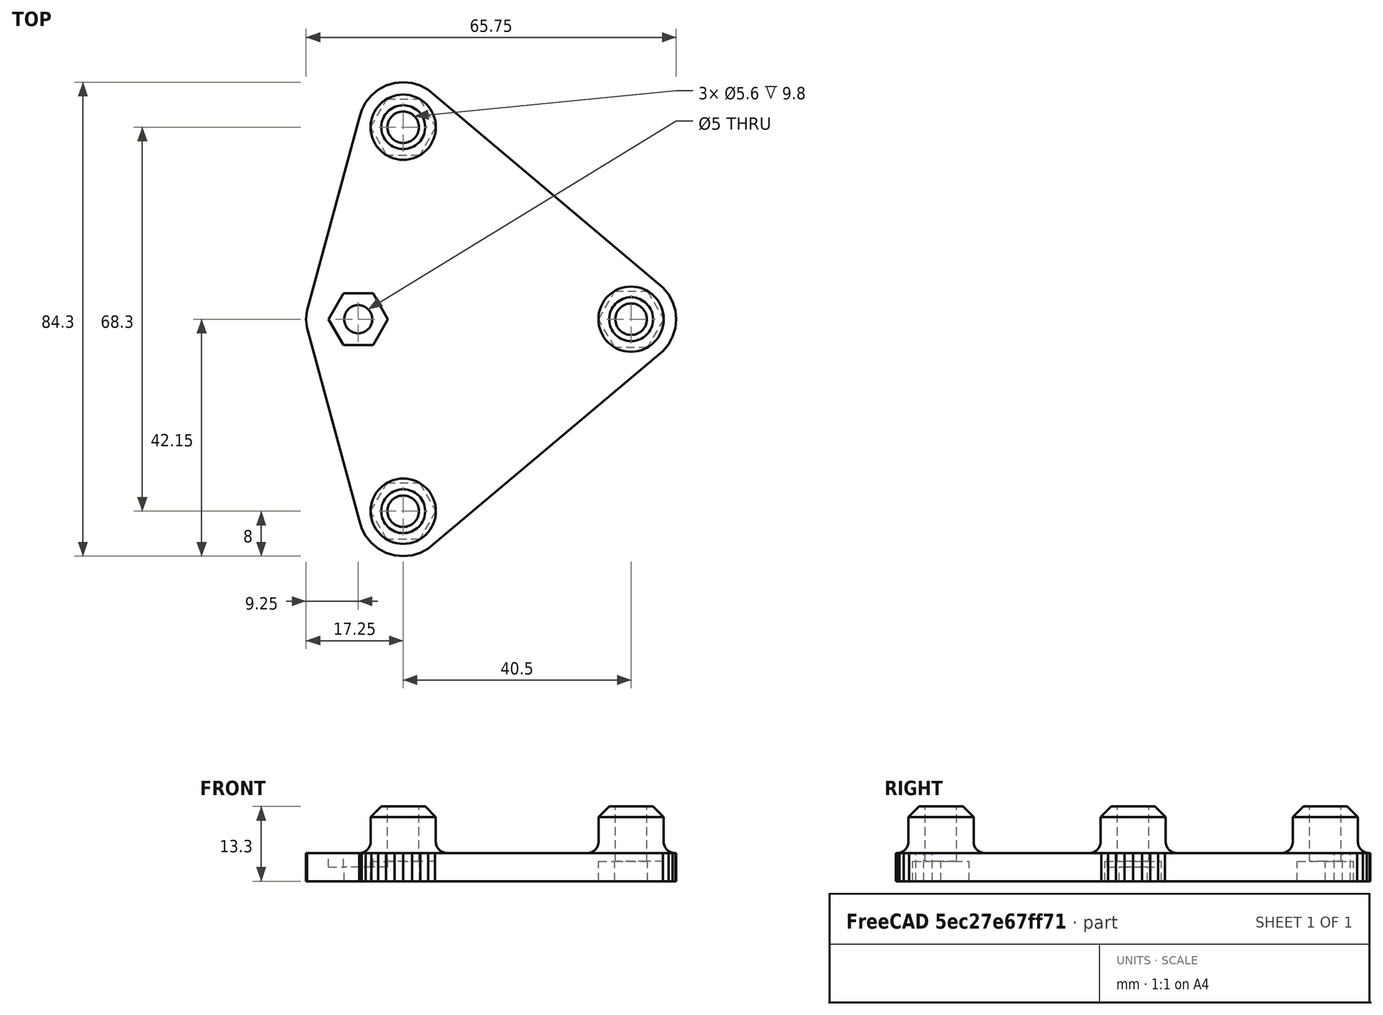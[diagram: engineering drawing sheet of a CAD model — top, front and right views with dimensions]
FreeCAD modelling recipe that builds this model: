
FCSTD DOCUMENT  (FreeCAD 0.19R24267 +99 (Git))
Label: carroZ_3_V1
License: All rights reserved
LicenseURL: http://en.wikipedia.org/wiki/All_rights_reserved
objects: Part::Feature×37, Part::Cylinder×7, Part::Cut×5, Part::Part2DObjectPython×4, Part::MultiFuse×4, Part::Prism×4, Part::Chamfer×3, Part::Fillet×3, Part::FeaturePython×2, Part::Extrusion×1, Part::Box×1, Part::Common×1, App::DocumentObjectGroupPython×1, Part::Refine×1
note: 73 computed .brp shape members not serialized (recipe doc carries the construction recipe); baked Part::Feature solids carry a one-line shape summary decoded from their .brp

FEATURE [Part::Feature] polygon
  shape: bbox 49.75 x 68.3 x 2e-07 mm, 1 faces, 0 solids (baked)
FEATURE [Part::Part2DObjectPython] circle  # Draft 2D object (typed FeaturePython)
  Area = 201.062
  FirstAngle = 0
  LastAngle = 0
  MakeFace = true
  Radius = 8
FEATURE [Part::FeaturePython] minkowski  # WARN: FeaturePython — macro-defined, semantics opaque (R4)
  Arguments = {'convexity': '0'}
  Children = -> [polygon,circle]
  Operation = minkowski
FEATURE [Part::Part2DObjectPython] circle001  # Draft 2D object (typed FeaturePython)
  Area = 24.6301
  FirstAngle = 0
  LastAngle = 0
  MakeFace = true
  Placement = pos=(-20.25,-34.15,0) rot=(0,0,1;0rad)
  Radius = 2.8
FEATURE [Part::Part2DObjectPython] circle002  # Draft 2D object (typed FeaturePython)
  Area = 24.6301
  FirstAngle = 0
  LastAngle = 0
  MakeFace = true
  Placement = pos=(-20.25,34.15,0) rot=(0,0,1;0rad)
  Radius = 2.8
FEATURE [Part::Part2DObjectPython] circle003  # Draft 2D object (typed FeaturePython)
  Area = 24.6301
  FirstAngle = 0
  LastAngle = 0
  MakeFace = true
  Placement = pos=(20.25,0,0) rot=(0,0,1;0rad)
  Radius = 2.8
FEATURE [Part::MultiFuse] union
  Shapes = -> [circle001,circle002,circle003]
FEATURE [Part::Cut] difference
  Base = -> minkowski
  Tool = -> union
FEATURE [Part::FeaturePython] RefineLinearExtrude  # WARN: FeaturePython — macro-defined, semantics opaque (R4)
  Base = -> difference
FEATURE [Part::Extrusion] LinearExtrude
  Base = -> RefineLinearExtrude
  Dir = (0,0,5)
  DirMode = 0
  FaceMakerClass = Part::FaceMakerBullseye
  LengthFwd = 0
  LengthRev = 0
  Solid = false
  Symmetric = false
FEATURE [Part::Cylinder] cylinder
  Angle = 360
  AttacherType = Attacher::AttachEngine3D
  Height = 13.3
  Radius = 5.8
FEATURE [Part::Cylinder] cylinder001
  Angle = 360
  AttacherType = Attacher::AttachEngine3D
  Height = 53.2
  Placement = pos=(0,0,-26.6) rot=(0,0,1;0rad)
  Radius = 2.8
FEATURE [Part::Cut] difference001
  Base = -> cylinder
  Placement = pos=(-20.25,-34.15,0) rot=(0,0,1;0rad)
  Tool = -> cylinder001
FEATURE [Part::Cylinder] cylinder002
  Angle = 360
  AttacherType = Attacher::AttachEngine3D
  Height = 13.3
  Radius = 5.8
FEATURE [Part::Cylinder] cylinder003
  Angle = 360
  AttacherType = Attacher::AttachEngine3D
  Height = 53.2
  Placement = pos=(0,0,-26.6) rot=(0,0,1;0rad)
  Radius = 2.8
FEATURE [Part::Cut] difference002
  Base = -> cylinder002
  Placement = pos=(-20.25,34.15,0) rot=(0,0,1;0rad)
  Tool = -> cylinder003
FEATURE [Part::Cylinder] cylinder004
  Angle = 360
  AttacherType = Attacher::AttachEngine3D
  Height = 13.3
  Radius = 5.8
FEATURE [Part::Cylinder] cylinder005
  Angle = 360
  AttacherType = Attacher::AttachEngine3D
  Height = 53.2
  Placement = pos=(0,0,-26.6) rot=(0,0,1;0rad)
  Radius = 2.8
FEATURE [Part::Cut] difference003
  Base = -> cylinder004
  Placement = pos=(20.25,0,0) rot=(0,0,1;0rad)
  Tool = -> cylinder005
FEATURE [Part::MultiFuse] union001
  Shapes = -> [LinearExtrude,difference001,difference002,difference003]
FEATURE [Part::Prism] prism
  AttacherType = Attacher::AttachEngine3D
  Circumradius = 5.79
  FirstAngle = 0
  Height = 7
  Placement = pos=(-20.25,-34.15,-3.5) rot=(0,0,1;0rad)
  Polygon = 6
  SecondAngle = 0
FEATURE [Part::Prism] prism001
  AttacherType = Attacher::AttachEngine3D
  Circumradius = 5.79
  FirstAngle = 0
  Height = 7
  Placement = pos=(-20.25,34.15,-3.5) rot=(0,0,1;0rad)
  Polygon = 6
  SecondAngle = 0
FEATURE [Part::Prism] prism002
  AttacherType = Attacher::AttachEngine3D
  Circumradius = 5.79
  FirstAngle = 0
  Height = 7
  Placement = pos=(20.25,0,-3.5) rot=(0,0,1;0rad)
  Polygon = 6
  SecondAngle = 0
FEATURE [Part::MultiFuse] Group
  Shapes = -> [prism,prism001,prism002]
FEATURE [Part::Cylinder] cylinder006
  Angle = 360
  AttacherType = Attacher::AttachEngine3D
  Height = 100
  Placement = pos=(-28.25,0,-47.5) rot=(0,0,1;0rad)
  Radius = 2.5
FEATURE [Part::Prism] prism003
  AttacherType = Attacher::AttachEngine3D
  Circumradius = 5.29
  FirstAngle = 0
  Height = 100
  Placement = pos=(-28.25,0,2.5) rot=(0,0,1;0rad)
  Polygon = 6
  SecondAngle = 0
FEATURE [Part::MultiFuse] union002
  Shapes = -> [Group,cylinder006,prism003]
FEATURE [Part::Cut] difference004
  Base = -> union001
  Tool = -> union002
FEATURE [Part::Box] cube
  AttacherType = Attacher::AttachEngine3D
  Height = 200
  Length = 200
  Placement = pos=(-100,-100,-100) rot=(0,0,1;0rad)
  Width = 200
FEATURE [Part::Common] intersection
  Base = -> difference004
  Tool = -> cube
FEATURE [App::DocumentObjectGroupPython] LayerContainer  label="Capas"  # scripted group (container) (typed FeaturePython)
FEATURE [Part::Feature] Line
  shape: bbox 1.561 x 0.1533 x 2e-07 mm, 0 faces, 0 solids (baked)
FEATURE [Part::Feature] Line001
  shape: bbox 1.561 x 0.1533 x 2e-07 mm, 0 faces, 0 solids (baked)
FEATURE [Part::Feature] Line002
  shape: bbox 1.501 x 0.4561 x 2e-07 mm, 0 faces, 0 solids (baked)
FEATURE [Part::Feature] Line003
  shape: bbox 1.383 x 0.7392 x 2e-07 mm, 0 faces, 0 solids (baked)
FEATURE [Part::Feature] Line004
  shape: bbox 1.213 x 0.9942 x 2e-07 mm, 0 faces, 0 solids (baked)
FEATURE [Part::Feature] Line005
  shape: bbox 0.9942 x 1.213 x 2e-07 mm, 0 faces, 0 solids (baked)
FEATURE [Part::Feature] Line006
  shape: bbox 0.7392 x 1.383 x 2e-07 mm, 0 faces, 0 solids (baked)
FEATURE [Part::Feature] Line007
  shape: bbox 0.4561 x 1.501 x 2e-07 mm, 0 faces, 0 solids (baked)
FEATURE [Part::Feature] Line008
  shape: bbox 9.25 x 34.15 x 2e-07 mm, 0 faces, 0 solids (baked)
FEATURE [Part::Feature] Line009
  shape: bbox 0.1533 x 1.561 x 2e-07 mm, 0 faces, 0 solids (baked)
FEATURE [Part::Feature] Line010
  shape: bbox 0.1533 x 1.561 x 2e-07 mm, 0 faces, 0 solids (baked)
FEATURE [Part::Feature] Line011
  shape: bbox 9.25 x 34.15 x 2e-07 mm, 0 faces, 0 solids (baked)
FEATURE [Part::Feature] Line012
  shape: bbox 0.4561 x 1.501 x 2e-07 mm, 0 faces, 0 solids (baked)
FEATURE [Part::Feature] Line013
  shape: bbox 0.7392 x 1.383 x 2e-07 mm, 0 faces, 0 solids (baked)
FEATURE [Part::Feature] Line014
  shape: bbox 0.9942 x 1.213 x 2e-07 mm, 0 faces, 0 solids (baked)
FEATURE [Part::Feature] Line015
  shape: bbox 1.213 x 0.9942 x 2e-07 mm, 0 faces, 0 solids (baked)
FEATURE [Part::Feature] Line016
  shape: bbox 1.383 x 0.7392 x 2e-07 mm, 0 faces, 0 solids (baked)
FEATURE [Part::Feature] Line017
  shape: bbox 1.501 x 0.4561 x 2e-07 mm, 0 faces, 0 solids (baked)
FEATURE [Part::Feature] Line018
  shape: bbox 1.561 x 0.1533 x 2e-07 mm, 0 faces, 0 solids (baked)
FEATURE [Part::Feature] Line019
  shape: bbox 1.561 x 0.1533 x 2e-07 mm, 0 faces, 0 solids (baked)
FEATURE [Part::Feature] Line020
  shape: bbox 1.501 x 0.4561 x 2e-07 mm, 0 faces, 0 solids (baked)
FEATURE [Part::Feature] Line021
  shape: bbox 1.383 x 0.7392 x 2e-07 mm, 0 faces, 0 solids (baked)
FEATURE [Part::Feature] Line022
  shape: bbox 1.213 x 0.9942 x 2e-07 mm, 0 faces, 0 solids (baked)
FEATURE [Part::Feature] Line023
  shape: bbox 40.5 x 34.15 x 2e-07 mm, 0 faces, 0 solids (baked)
FEATURE [Part::Feature] Line024
  shape: bbox 0.9942 x 1.213 x 2e-07 mm, 0 faces, 0 solids (baked)
FEATURE [Part::Feature] Line025
  shape: bbox 0.7392 x 1.383 x 2e-07 mm, 0 faces, 0 solids (baked)
FEATURE [Part::Feature] Line026
  shape: bbox 0.4561 x 1.501 x 2e-07 mm, 0 faces, 0 solids (baked)
FEATURE [Part::Feature] Line027
  shape: bbox 0.1533 x 1.561 x 2e-07 mm, 0 faces, 0 solids (baked)
FEATURE [Part::Feature] Line028
  shape: bbox 0.1533 x 1.561 x 2e-07 mm, 0 faces, 0 solids (baked)
FEATURE [Part::Feature] Line029
  shape: bbox 0.4561 x 1.501 x 2e-07 mm, 0 faces, 0 solids (baked)
FEATURE [Part::Feature] Line030
  shape: bbox 0.7392 x 1.383 x 2e-07 mm, 0 faces, 0 solids (baked)
FEATURE [Part::Feature] Line031
  shape: bbox 0.9942 x 1.213 x 2e-07 mm, 0 faces, 0 solids (baked)
FEATURE [Part::Feature] Line032
  shape: bbox 40.5 x 34.15 x 2e-07 mm, 0 faces, 0 solids (baked)
FEATURE [Part::Feature] Line033
  shape: bbox 1.213 x 0.9942 x 2e-07 mm, 0 faces, 0 solids (baked)
FEATURE [Part::Feature] Line034
  shape: bbox 1.383 x 0.7392 x 2e-07 mm, 0 faces, 0 solids (baked)
FEATURE [Part::Feature] Line035
  shape: bbox 1.501 x 0.4561 x 2e-07 mm, 0 faces, 0 solids (baked)
FEATURE [Part::Refine] intersection001
  Source = -> intersection
FEATURE [Part::Chamfer] Chamfer
  Base = -> intersection001
  Edges = 1 edges r=1.9: [Edge119]
FEATURE [Part::Chamfer] Chamfer001
  Base = -> Chamfer
  Edges = 1 edges r=1.9: [Edge138]
FEATURE [Part::Chamfer] Chamfer002
  Base = -> Chamfer001
  Edges = 1 edges r=1.9: [Edge138]
FEATURE [Part::Fillet] Fillet
  Base = -> Chamfer002
  Edges = 1 edges r=2: [Edge3]
FEATURE [Part::Fillet] Fillet001
  Base = -> Fillet
  Edges = 1 edges r=2: [Edge51]
FEATURE [Part::Fillet] Fillet002
  Base = -> Fillet001
  Edges = 1 edges r=2: [Edge39]
